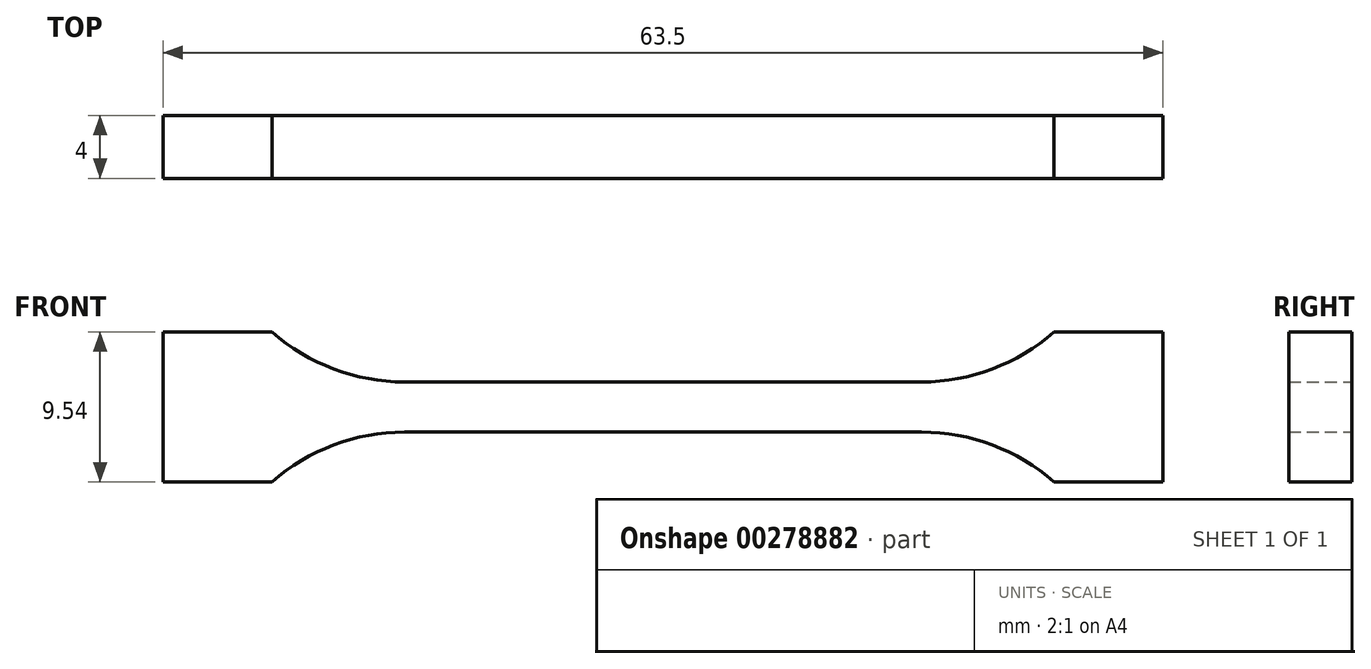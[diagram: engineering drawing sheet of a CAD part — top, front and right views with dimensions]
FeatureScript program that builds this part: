
annotation { "Feature Type Name" : "Feature", "Feature Type Description" : "" }
export const myFeature = defineFeature(function(context is Context, id is Id, definition is map)
    precondition{}
    {
        {
            var Q0;
            Q0=qCreatedBy(makeId("Front.planeOp"),FACE);
            var sketch = newSketch(context, id + "F0", { "sketchPlane" : qUnion([Q0])});
            skLineSegment(sketch, "E0", {"start": v(0, 1.6) * mm, "end": v(16.43, 1.6) * mm});
            skArc(sketch, "E1", {"start": v(16.43, 1.6) * mm, "mid": v(20.92, 2.41) * mm, "end": v(24.83, 4.77) * mm});
            skLineSegment(sketch, "E2", {"start": v(24.83, 4.77) * mm, "end": v(31.75, 4.77) * mm});
            skLineSegment(sketch, "E3.MirrorCS", {"start": v(24.83, -4.76) * mm, "end": v(31.75, -4.76) * mm});
            skLineSegment(sketch, "E4.MirrorCS", {"start": v(0, -1.6) * mm, "end": v(16.43, -1.6) * mm});
            skArc(sketch, "E5.MirrorCS", {"start": v(16.43, -1.6) * mm, "mid": v(20.92, -2.41) * mm, "end": v(24.83, -4.77) * mm});
            skArc(sketch, "E6.MirrorCS", {"start": v(-16.43, -1.6) * mm, "mid": v(-20.92, -2.41) * mm, "end": v(-24.83, -4.77) * mm});
            skLineSegment(sketch, "E7.MirrorCS", {"start": v(0, 1.6) * mm, "end": v(-16.43, 1.59) * mm});
            skArc(sketch, "E8.MirrorCS", {"start": v(-16.43, 1.6) * mm, "mid": v(-20.92, 2.41) * mm, "end": v(-24.83, 4.77) * mm});
            skLineSegment(sketch, "E9.MirrorCS", {"start": v(-24.83, -4.77) * mm, "end": v(-31.75, -4.77) * mm});
            skLineSegment(sketch, "E10.MirrorCS", {"start": v(0, -1.59) * mm, "end": v(-16.43, -1.6) * mm});
            skLineSegment(sketch, "E11.MirrorCS", {"start": v(-24.83, 4.76) * mm, "end": v(-31.75, 4.76) * mm});
            skLineSegment(sketch, "E12", {"start": v(-31.75, 4.77) * mm, "end": v(-31.75, -4.77) * mm});
            skLineSegment(sketch, "E13", {"start": v(31.75, 4.77) * mm, "end": v(31.75, -4.77) * mm});
            skSolve(sketch);
        }
        {
            var Q0;
            Q0 = qSketchRegion(id + "F0", true);
            extrude(context, id + "F1", {"entities" : qUnion([Q0]), "endBound" : BoundingType.SYMMETRIC, "depth" : 4 * mm});
        }
    });
